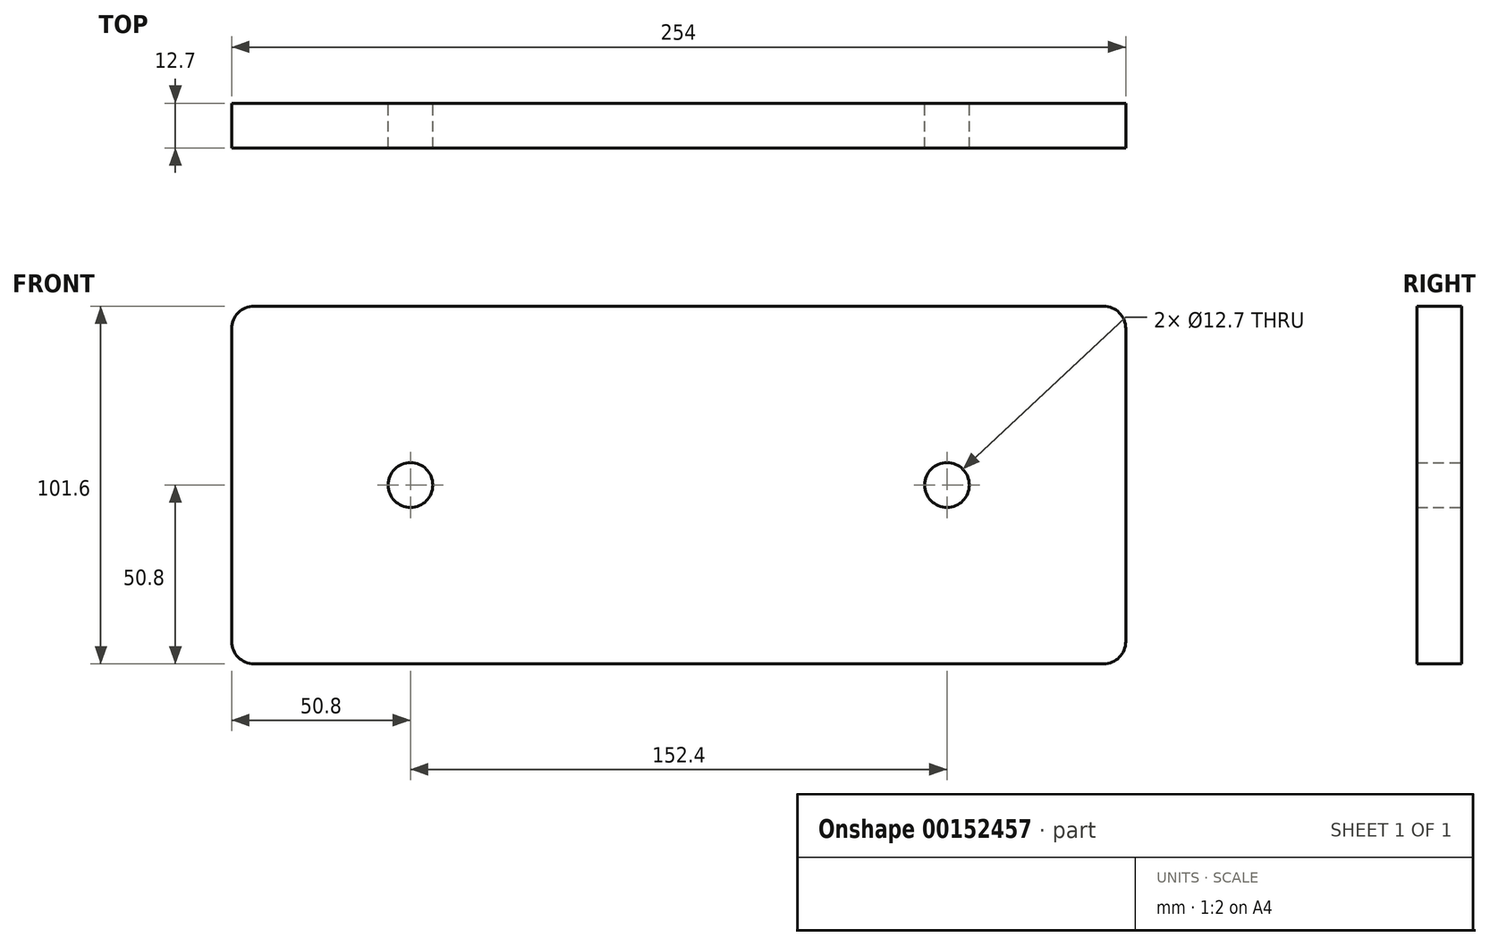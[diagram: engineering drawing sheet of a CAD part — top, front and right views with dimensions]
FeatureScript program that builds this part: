
annotation { "Feature Type Name" : "Feature", "Feature Type Description" : "" }
export const myFeature = defineFeature(function(context is Context, id is Id, definition is map)
    precondition{}
    {
        {
            var Q0;
            Q0=qCreatedBy(makeId("Front.planeOp"),FACE);
            var sketch = newSketch(context, id + "F0", { "sketchPlane" : qUnion([Q0])});
            skLineSegment(sketch, "E0.bottom", {"start": v(-6.35, 0) * mm, "end": v(-247.65, 0) * mm});
            skLineSegment(sketch, "E0.top", {"start": v(-6.35, 101.6) * mm, "end": v(-247.65, 101.6) * mm});
            skLineSegment(sketch, "E0.left", {"start": v(0, 6.35) * mm, "end": v(0, 95.25) * mm});
            skLineSegment(sketch, "E0.right", {"start": v(-254, 6.35) * mm, "end": v(-254, 95.25) * mm});
            skCircle(sketch, "E1", {"center": v(-203.2, 50.8) * mm, "radius": 6.35 * mm});
            skPoint(sketch, "E1.centerSnap0", {"position": v(-254, 50.8) * mm});
            skCircle(sketch, "E2", {"center": v(-50.8, 50.8) * mm, "radius": 6.35 * mm});
            skPoint(sketch, "E3.visualSharp", {"position": v(0, 101.6) * mm});
            skArc(sketch, "E3.filletArc", {"start": v(0, 95.25) * mm, "mid": v(-1.86, 99.74) * mm, "end": v(-6.35, 101.6) * mm});
            skPoint(sketch, "E4.visualSharp", {"position": v(0, 0) * mm});
            skArc(sketch, "E4.filletArc", {"start": v(-6.35, 0) * mm, "mid": v(-1.86, 1.86) * mm, "end": v(0, 6.35) * mm});
            skPoint(sketch, "E5.visualSharp", {"position": v(-254, 0) * mm});
            skArc(sketch, "E5.filletArc", {"start": v(-254, 6.35) * mm, "mid": v(-252.14, 1.86) * mm, "end": v(-247.65, 0) * mm});
            skPoint(sketch, "E6.visualSharp", {"position": v(-254, 101.6) * mm});
            skArc(sketch, "E6.filletArc", {"start": v(-247.65, 101.6) * mm, "mid": v(-252.14, 99.74) * mm, "end": v(-254, 95.25) * mm});
            skSolve(sketch);
        }
        {
            var Q0;
            Q0 = qSketchRegion(id + "F0", true);
            extrude(context, id + "F1", {"entities" : qUnion([Q0]), "depth" : 12.7 * mm});
        }
    });
